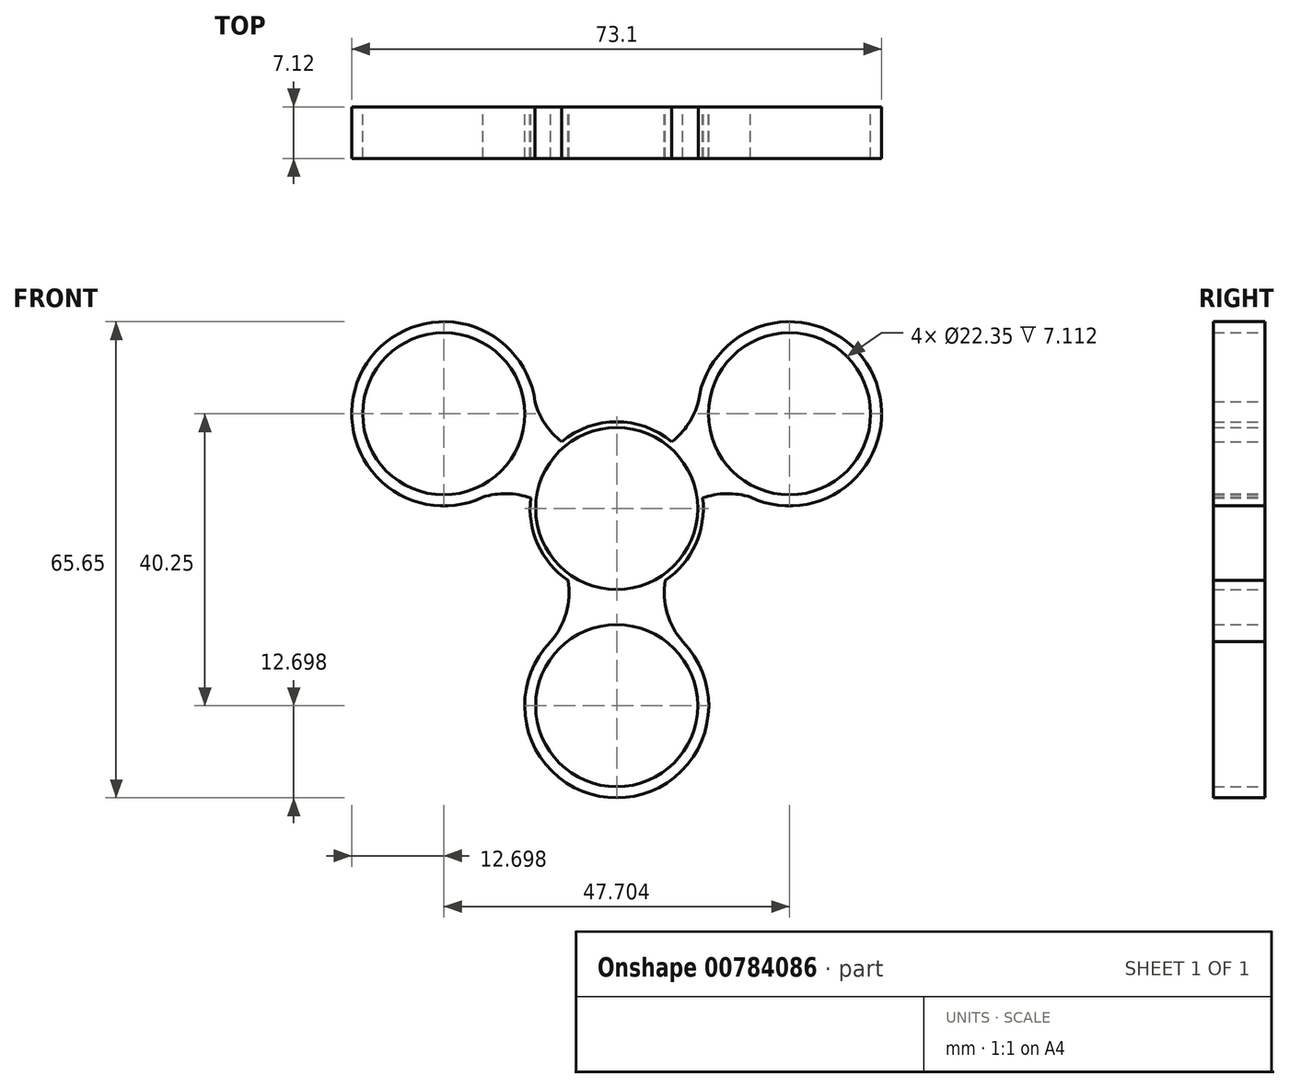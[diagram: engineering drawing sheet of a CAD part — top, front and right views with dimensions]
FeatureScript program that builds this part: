
annotation { "Feature Type Name" : "Feature", "Feature Type Description" : "" }
export const myFeature = defineFeature(function(context is Context, id is Id, definition is map)
    precondition{}
    {
        {
            var Q0;
            Q0=qCreatedBy(makeId("Front.planeOp"),FACE);
            var sketch = newSketch(context, id + "F0", { "sketchPlane" : qUnion([Q0])});
            skCircle(sketch, "E0", {"center": v(0, 0) * mm, "radius": 11.95 * mm});
            skCircle(sketch, "E1.MirrorC", {"center": v(23.85, 13.06) * mm, "radius": 12.7 * mm});
            skLineSegment(sketch, "E2", {"start": v(0, 0) * mm, "end": v(23.85, 13.06) * mm});
            skCircle(sketch, "E3.MirrorC", {"center": v(0, -27.2) * mm, "radius": 12.7 * mm});
            skArc(sketch, "E4.MirrorCS", {"start": v(32.98, -18.98) * mm, "mid": v(32.23, -16.44) * mm, "end": v(32.24, -13.8) * mm});
            skArc(sketch, "E5.MirrorCS", {"start": v(-6.7, -9.9) * mm, "mid": v(-7.02, -14.64) * mm, "end": v(-9.46, -18.72) * mm});
            skLineSegment(sketch, "E6", {"start": v(0, 36.4) * mm, "end": v(0, -27.2) * mm});
            skArc(sketch, "E7.MirrorCS", {"start": v(6.7, -9.9) * mm, "mid": v(7.02, -14.64) * mm, "end": v(9.46, -18.72) * mm});
            skArc(sketch, "E8", {"start": v(7.6, 9.22) * mm, "mid": v(10.27, 12.28) * mm, "end": v(11.53, 16.14) * mm});
            skArc(sketch, "E9.MirrorCS", {"start": v(11.87, 1.44) * mm, "mid": v(15.88, 2.04) * mm, "end": v(19.81, 1.02) * mm});
            skArc(sketch, "E10.MirrorCS", {"start": v(-7.6, 9.22) * mm, "mid": v(-10.27, 12.28) * mm, "end": v(-11.53, 16.14) * mm});
            skArc(sketch, "E11.MirrorCS", {"start": v(-11.87, 1.44) * mm, "mid": v(-15.88, 2.04) * mm, "end": v(-19.81, 1.02) * mm});
            skCircle(sketch, "E12.MirrorC", {"center": v(-23.85, 13.06) * mm, "radius": 12.7 * mm});
            skCircle(sketch, "E13", {"center": v(23.85, 13.06) * mm, "radius": 11.18 * mm});
            skCircle(sketch, "E14", {"center": v(0, -27.2) * mm, "radius": 11.18 * mm});
            skCircle(sketch, "E15", {"center": v(0, 0) * mm, "radius": 11.18 * mm});
            skCircle(sketch, "E16", {"center": v(-23.85, 13.06) * mm, "radius": 11.18 * mm});
            skPoint(sketch, "E17", {"position": v(-30.69, 2.36) * mm});
            skSolve(sketch);
        }
        {
            var Q0;
            Q0 = qSketchRegion(id + "F0", true);
            extrude(context, id + "F1", {"entities" : qUnion([Q0]), "endBound" : BoundingType.SYMMETRIC, "depth" : 7.11 * mm, "offsetDistance" : 25.4 * mm});
        }
    });
